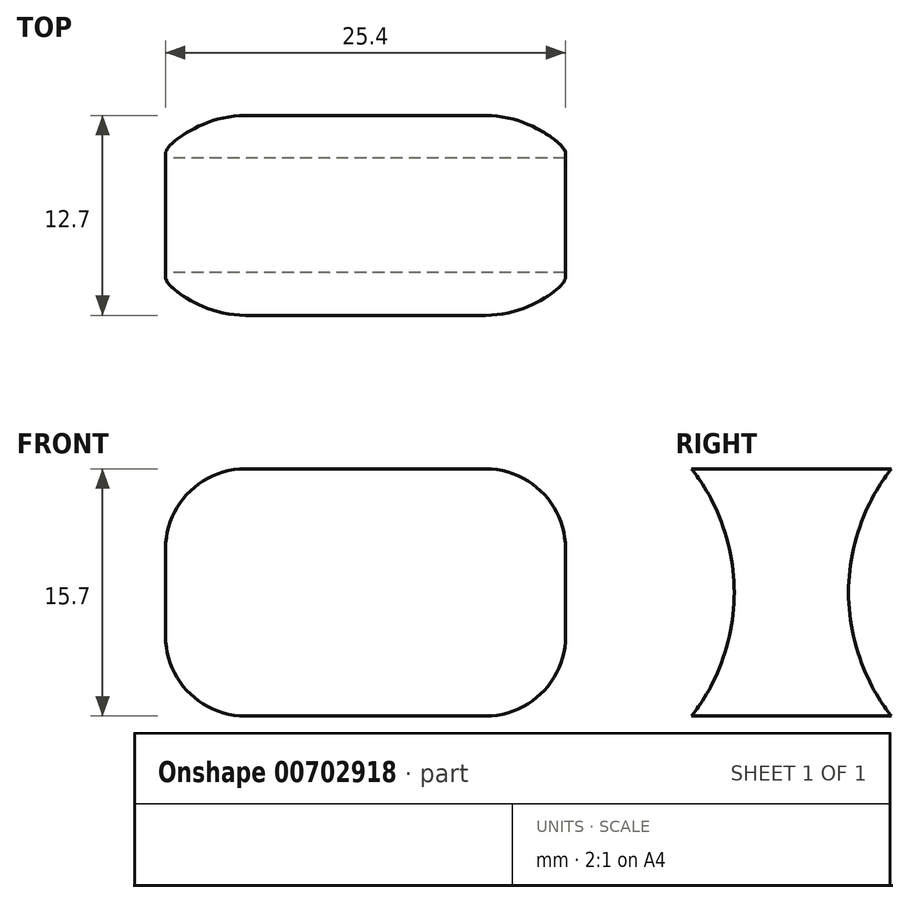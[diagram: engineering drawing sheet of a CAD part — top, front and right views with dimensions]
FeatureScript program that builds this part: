
annotation { "Feature Type Name" : "Feature", "Feature Type Description" : "" }
export const myFeature = defineFeature(function(context is Context, id is Id, definition is map)
    precondition{}
    {
        {
            var Q0;
            Q0=qCreatedBy(makeId("Right.planeOp"),FACE);
            var sketch = newSketch(context, id + "F0", { "sketchPlane" : qUnion([Q0])});
            skLineSegment(sketch, "E0.bottom", {"start": v(-6.35, 7.85) * mm, "end": v(6.35, 7.85) * mm});
            skLineSegment(sketch, "E0.top", {"start": v(-6.35, -7.85) * mm, "end": v(6.35, -7.85) * mm});
            skPoint(sketch, "E0.middle", {"position": v(0, 0) * mm});
            skArc(sketch, "E1", {"start": v(-6.35, 7.85) * mm, "mid": v(-3.63, 0) * mm, "end": v(-6.35, -7.85) * mm});
            skArc(sketch, "E2", {"start": v(6.35, 7.85) * mm, "mid": v(3.63, 0) * mm, "end": v(6.35, -7.85) * mm});
            skSolve(sketch);
        }
        {
            var Q0;
            Q0 = qSketchRegion(id + "F0", true);
            extrude(context, id + "F1", {"entities" : qUnion([Q0]), "endBound" : BoundingType.SYMMETRIC, "depth" : 25.4 * mm, "offsetDistance" : 25.4 * mm});
        }
        {
            var Q0;
            Q0=makeQuery(id+"F1.opExtrude","CAP_EDGE",EDGE,{"disambiguationData":[OSD([sQuery(id+"F0.wireOp",EDGE,"E0.bottom")])],"isStart":true});
            var Q1;
            Q1=makeQuery(id+"F1.opExtrude","CAP_EDGE",EDGE,{"disambiguationData":[OSD([sQuery(id+"F0.wireOp",EDGE,"E0.top")])],"isStart":true});
            var Q2;
            Q2=makeQuery(id+"F1.opExtrude","CAP_EDGE",EDGE,{"disambiguationData":[OSD([sQuery(id+"F0.wireOp",EDGE,"E0.bottom")])],"isStart":false});
            var Q3;
            Q3=makeQuery(id+"F1.opExtrude","CAP_EDGE",EDGE,{"disambiguationData":[OSD([sQuery(id+"F0.wireOp",EDGE,"E0.top")])],"isStart":false});
            fillet(context, id + "F2", {"entities" : qUnion([Q0, Q1, Q2, Q3]), "radius" : 5.08 * mm, "tangentPropagation" : true, "allowEdgeOverflow" : false});
        }
    });
